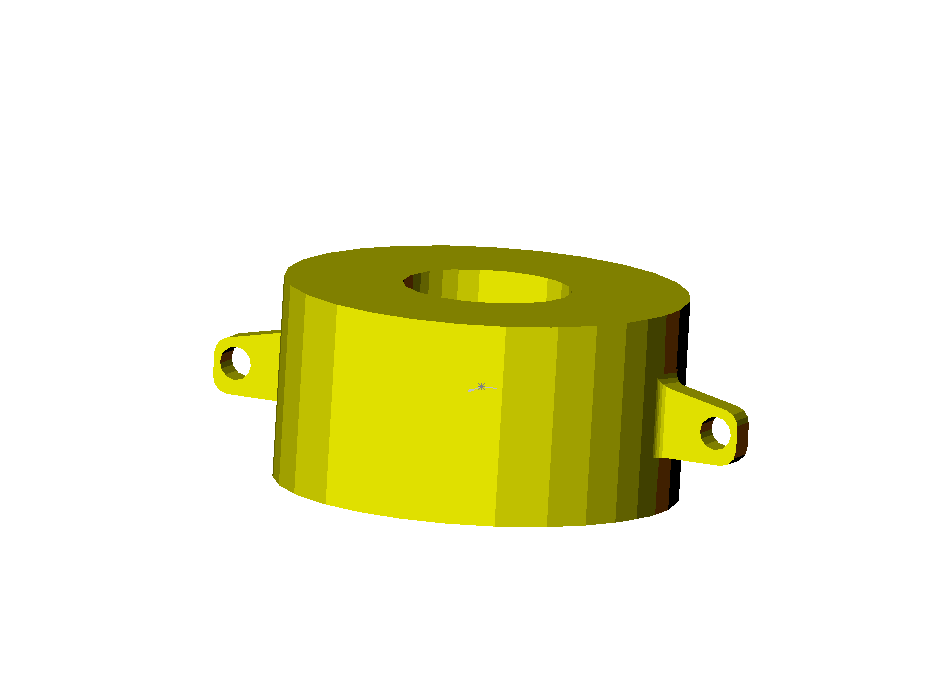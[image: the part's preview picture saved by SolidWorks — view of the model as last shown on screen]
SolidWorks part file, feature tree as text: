
SOLIDWORKS PART (.sldprt)
format: sldprt  version: not decoded by parser v0  size: 150,528 bytes
history: native  units: mm
features: sketch x4, fillet x4, plane x3, extrude x2, mirror x2, cut_extrude x2, material x1 (+9 scaffold rows collapsed)
feature tree (27):
  scaffold x9  (default folders/planes/origin — collapsed)
  material  "Material <not specified>"
  plane  "Plane1"
  plane  "Plane2"
  plane  "Plane3"
  sketch  "Sketch1"  dims[D1=120.0mm]
  extrude  "Base-Extrude"  Depth=60mm
  sketch  "Sketch2"  dims[c1.D1=16.0mm c1.D2=20.0mm c2.D1=55.0mm c2.D2=16.0mm c2.D3=12.5mm c2.D4=22.5mm c2.D5=~30.696091mm]
  extrude  "Boss-Extrude1"  Depth=8mm
  fillet  "Fillet1"  Radius=4mm
  mirror  "Mirror1"
  fillet  "Fillet2"  Radius=4mm
  sketch  "Sketch3"  dims[D1=50.0mm]
  sketch  "Sketch5"  dims[c1.D1=10.0mm c1.D2=5.0mm c1.D3=5.0mm c1.D4=5.0mm c2.D2=3.0mm c2.D3=78.0mm]
  cut_extrude  "Cut-Extrude1"  [1 undecoded]
  mirror  "Mirror2"
  cut_extrude  "Cut-Extrude2"  [1 undecoded]
  fillet  "Fillet5"  Radius=5mm
  fillet  "Fillet7"  Radius=5mm
decode coverage: 10 of 14 modeling features carry decoded parameters
note: ~ marks probable driven/reference dimensions
note: 2 parameter values undecoded
note: suppression state not decoded; provenance and decode notes live in map.json
